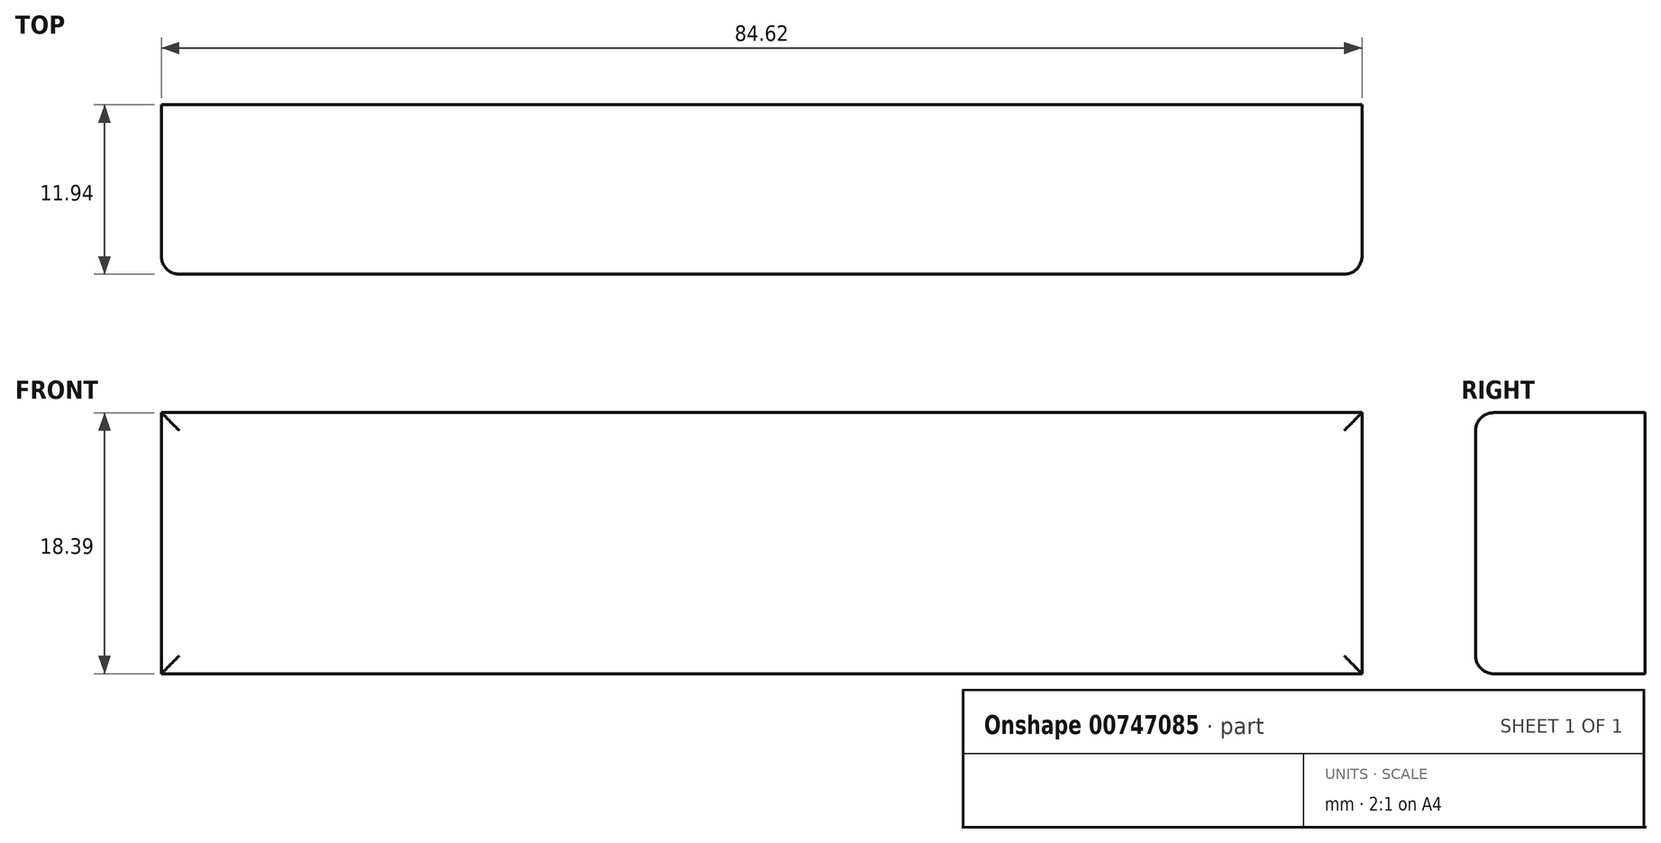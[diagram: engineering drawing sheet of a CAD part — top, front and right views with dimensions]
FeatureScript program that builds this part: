
annotation { "Feature Type Name" : "Feature", "Feature Type Description" : "" }
export const myFeature = defineFeature(function(context is Context, id is Id, definition is map)
    precondition{}
    {
        {
            var Q0;
            Q0=qCreatedBy(makeId("Front.planeOp"),FACE);
            var sketch = newSketch(context, id + "F0", { "sketchPlane" : qUnion([Q0])});
            skLineSegment(sketch, "E0.bottom", {"start": v(0, 0) * mm, "end": v(-84.62, 0) * mm});
            skLineSegment(sketch, "E0.top", {"start": v(0, 18.4) * mm, "end": v(-84.62, 18.4) * mm});
            skLineSegment(sketch, "E0.left", {"start": v(0, 0) * mm, "end": v(0, 18.4) * mm});
            skLineSegment(sketch, "E0.right", {"start": v(-84.62, 0) * mm, "end": v(-84.62, 18.4) * mm});
            skSolve(sketch);
        }
        {
            var Q0;
            Q0=makeQuery(id+"F0.imprint","IMPRINT",FACE,{"disambiguationData":[TD([[makeQuery(id+"F0.imprint","IMPRINT",EDGE,{"derivedFrom":sQuery(id+"F0.wireOp",EDGE,"E0.bottom")}),-1.0]])]});
            extrude(context, id + "F1", {"entities" : qUnion([Q0]), "depth" : 11.94 * mm, "offsetDistance" : 25.4 * mm});
        }
        {
            var Q0;
            Q0=makeQuery(id+"F1.opExtrude","CAP_EDGE",EDGE,{"disambiguationData":[OSD([sQuery(id+"F0.wireOp",EDGE,"E0.top")])],"isStart":false});
            var Q1;
            Q1=makeQuery(id+"F1.opExtrude","CAP_EDGE",EDGE,{"disambiguationData":[OSD([sQuery(id+"F0.wireOp",EDGE,"E0.right")])],"isStart":false});
            var Q2;
            Q2=makeQuery(id+"F1.opExtrude","CAP_EDGE",EDGE,{"disambiguationData":[OSD([sQuery(id+"F0.wireOp",EDGE,"E0.bottom")])],"isStart":false});
            var Q3;
            Q3=makeQuery(id+"F1.opExtrude","CAP_FACE",FACE,{"disambiguationData":[OSD([sQuery(id+"F0.wireOp",EDGE,"E0.bottom"),sQuery(id+"F0.wireOp",EDGE,"E0.top"),sQuery(id+"F0.wireOp",EDGE,"E0.left"),sQuery(id+"F0.wireOp",EDGE,"E0.right")])],"isStart":false});
            fillet(context, id + "F2", {"entities" : qUnion([Q0, Q1, Q2, Q3]), "radius" : 1.27 * mm, "tangentPropagation" : true, "allowEdgeOverflow" : false});
        }
    });
